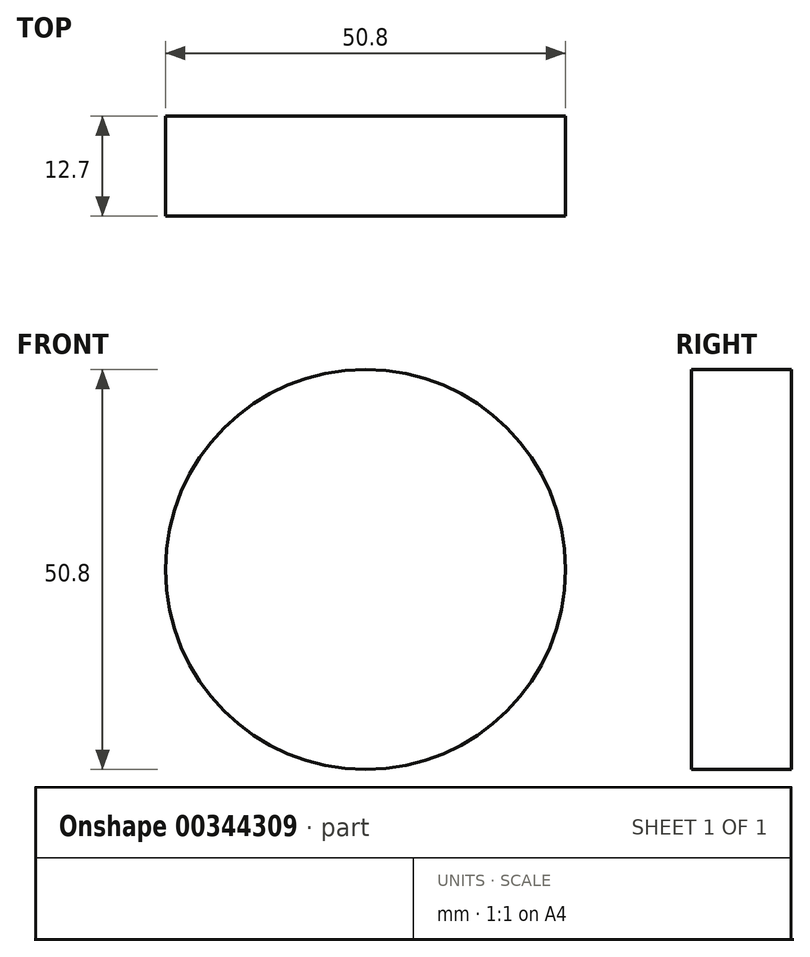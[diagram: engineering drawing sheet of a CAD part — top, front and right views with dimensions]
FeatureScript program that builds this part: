
annotation { "Feature Type Name" : "Feature", "Feature Type Description" : "" }
export const myFeature = defineFeature(function(context is Context, id is Id, definition is map)
    precondition{}
    {
        {
            var Q0;
            Q0=qCreatedBy(makeId("Front.planeOp"),FACE);
            var sketch = newSketch(context, id + "F0", { "sketchPlane" : qUnion([Q0])});
            skCircle(sketch, "E0", {"center": v(0, 0) * mm, "radius": 25.4 * mm});
            skCircle(sketch, "E1", {"center": v(0, 0) * mm, "radius": 16.51 * mm, "construction": true});
            skCircle(sketch, "E2", {"center": v(0, 0) * mm, "radius": 22.86 * mm, "construction": true});
            skLineSegment(sketch, "E3", {"start": v(0, 0) * mm, "end": v(0, 45.4) * mm, "construction": true});
            skLineSegment(sketch, "E4", {"start": v(0, 0) * mm, "end": v(12.17, 45.4) * mm, "construction": true});
            skLineSegment(sketch, "E5", {"start": v(0, 22.86) * mm, "end": v(0, 16.51) * mm});
            skLineSegment(sketch, "E6", {"start": v(5.92, 22.08) * mm, "end": v(4.27, 15.95) * mm});
            skArc(sketch, "E7", {"start": v(0, 22.86) * mm, "mid": v(2.98, 22.66) * mm, "end": v(5.92, 22.08) * mm});
            skArc(sketch, "E8", {"start": v(0, 16.51) * mm, "mid": v(2.15, 16.37) * mm, "end": v(4.27, 15.95) * mm});
            skLineSegment(sketch, "E9.1.0", {"start": v(-19.8, 11.43) * mm, "end": v(-14.3, 8.26) * mm});
            skLineSegment(sketch, "E9.1.1", {"start": v(-16.16, 16.16) * mm, "end": v(-11.67, 11.67) * mm});
            skArc(sketch, "E9.1.2", {"start": v(-19.8, 11.43) * mm, "mid": v(-18.14, 13.92) * mm, "end": v(-16.16, 16.16) * mm});
            skArc(sketch, "E9.1.3", {"start": v(-14.3, 8.26) * mm, "mid": v(-13.1, 10.05) * mm, "end": v(-11.67, 11.67) * mm});
            skLineSegment(sketch, "E9.2.0", {"start": v(-19.8, -11.43) * mm, "end": v(-14.3, -8.25) * mm});
            skLineSegment(sketch, "E9.2.1", {"start": v(-22.08, -5.92) * mm, "end": v(-15.95, -4.27) * mm});
            skArc(sketch, "E9.2.2", {"start": v(-19.8, -11.43) * mm, "mid": v(-21.12, -8.75) * mm, "end": v(-22.08, -5.92) * mm});
            skArc(sketch, "E9.2.3", {"start": v(-14.3, -8.25) * mm, "mid": v(-15.25, -6.32) * mm, "end": v(-15.95, -4.27) * mm});
            skLineSegment(sketch, "E9.3.0", {"start": v(0, -22.86) * mm, "end": v(0, -16.51) * mm});
            skLineSegment(sketch, "E9.3.1", {"start": v(-5.92, -22.08) * mm, "end": v(-4.27, -15.95) * mm});
            skArc(sketch, "E9.3.2", {"start": v(0, -22.86) * mm, "mid": v(-2.98, -22.66) * mm, "end": v(-5.92, -22.08) * mm});
            skArc(sketch, "E9.3.3", {"start": v(0, -16.51) * mm, "mid": v(-2.15, -16.37) * mm, "end": v(-4.27, -15.95) * mm});
            skLineSegment(sketch, "E9.4.0", {"start": v(19.8, -11.43) * mm, "end": v(14.3, -8.26) * mm});
            skLineSegment(sketch, "E9.4.1", {"start": v(16.16, -16.16) * mm, "end": v(11.67, -11.67) * mm});
            skArc(sketch, "E9.4.2", {"start": v(19.8, -11.43) * mm, "mid": v(18.14, -13.92) * mm, "end": v(16.16, -16.16) * mm});
            skArc(sketch, "E9.4.3", {"start": v(14.3, -8.26) * mm, "mid": v(13.1, -10.05) * mm, "end": v(11.67, -11.67) * mm});
            skLineSegment(sketch, "E9.5.0", {"start": v(19.8, 11.43) * mm, "end": v(14.3, 8.26) * mm});
            skLineSegment(sketch, "E9.5.1", {"start": v(22.08, 5.92) * mm, "end": v(15.95, 4.27) * mm});
            skArc(sketch, "E9.5.2", {"start": v(19.8, 11.43) * mm, "mid": v(21.12, 8.75) * mm, "end": v(22.08, 5.92) * mm});
            skArc(sketch, "E9.5.3", {"start": v(14.3, 8.26) * mm, "mid": v(15.25, 6.32) * mm, "end": v(15.95, 4.27) * mm});
            skSolve(sketch);
        }
        {
            var Q0;
            Q0=makeQuery(id+"F0.imprint","IMPRINT",FACE,{"disambiguationData":[TD([[makeQuery(id+"F0.imprint","IMPRINT",EDGE,{"derivedFrom":sQuery(id+"F0.wireOp",EDGE,"RZoZ2ge6-8GLw-KyjR-YQcm-iaacOE0NIIhm")}),-1.0]])]});
            var Q1;
            Q1=makeQuery(id+"F0.imprint","IMPRINT",FACE,{"disambiguationData":[TD([[makeQuery(id+"F0.imprint","IMPRINT",EDGE,{"derivedFrom":sQuery(id+"F0.wireOp",EDGE,"E0")}),1.0]])]});
            var Q2;
            Q2=makeQuery(id+"F0.imprint","IMPRINT",FACE,{"disambiguationData":[TD([[makeQuery(id+"F0.imprint","IMPRINT",EDGE,{"derivedFrom":sQuery(id+"F0.wireOp",EDGE,"E5")}),1.0]])]});
            var Q3;
            Q3=makeQuery(id+"F0.imprint","IMPRINT",FACE,{"disambiguationData":[TD([[makeQuery(id+"F0.imprint","IMPRINT",EDGE,{"derivedFrom":sQuery(id+"F0.wireOp",EDGE,"E9.1.0")}),1.0]])]});
            var Q4;
            Q4=makeQuery(id+"F0.imprint","IMPRINT",FACE,{"disambiguationData":[TD([[makeQuery(id+"F0.imprint","IMPRINT",EDGE,{"derivedFrom":sQuery(id+"F0.wireOp",EDGE,"E9.2.0")}),1.0]])]});
            var Q5;
            Q5=makeQuery(id+"F0.imprint","IMPRINT",FACE,{"disambiguationData":[TD([[makeQuery(id+"F0.imprint","IMPRINT",EDGE,{"derivedFrom":sQuery(id+"F0.wireOp",EDGE,"E9.4.0")}),1.0]])]});
            var Q6;
            Q6=makeQuery(id+"F0.imprint","IMPRINT",FACE,{"disambiguationData":[TD([[makeQuery(id+"F0.imprint","IMPRINT",EDGE,{"derivedFrom":sQuery(id+"F0.wireOp",EDGE,"E9.5.0")}),1.0]])]});
            var Q7;
            Q7=makeQuery(id+"F0.imprint","IMPRINT",FACE,{"disambiguationData":[TD([[makeQuery(id+"F0.imprint","IMPRINT",EDGE,{"derivedFrom":sQuery(id+"F0.wireOp",EDGE,"E9.3.0")}),1.0]])]});
            extrude(context, id + "F1", {"entities" : qUnion([Q0, Q1, Q2, Q3, Q4, Q5, Q6, Q7]), "depth" : 12.7 * mm});
        }
        {
            var Q0;
            Q0=makeQuery(id+"F0.imprint","IMPRINT",FACE,{"disambiguationData":[TD([[makeQuery(id+"F0.imprint","IMPRINT",EDGE,{"derivedFrom":sQuery(id+"F0.wireOp",EDGE,"E9.5.0")}),1.0]])]});
            var Q1;
            Q1=makeQuery(id+"F0.imprint","IMPRINT",FACE,{"disambiguationData":[TD([[makeQuery(id+"F0.imprint","IMPRINT",EDGE,{"derivedFrom":sQuery(id+"F0.wireOp",EDGE,"E9.4.0")}),1.0]])]});
            var Q2;
            Q2=makeQuery(id+"F0.imprint","IMPRINT",FACE,{"disambiguationData":[TD([[makeQuery(id+"F0.imprint","IMPRINT",EDGE,{"derivedFrom":sQuery(id+"F0.wireOp",EDGE,"E9.3.0")}),1.0]])]});
            var Q3;
            Q3=makeQuery(id+"F0.imprint","IMPRINT",FACE,{"disambiguationData":[TD([[makeQuery(id+"F0.imprint","IMPRINT",EDGE,{"derivedFrom":sQuery(id+"F0.wireOp",EDGE,"E9.1.0")}),1.0]])]});
            var Q4;
            Q4=makeQuery(id+"F0.imprint","IMPRINT",FACE,{"disambiguationData":[TD([[makeQuery(id+"F0.imprint","IMPRINT",EDGE,{"derivedFrom":sQuery(id+"F0.wireOp",EDGE,"E5")}),1.0]])]});
            var Q5;
            Q5=makeQuery(id+"F0.imprint","IMPRINT",FACE,{"disambiguationData":[TD([[makeQuery(id+"F0.imprint","IMPRINT",EDGE,{"derivedFrom":sQuery(id+"F0.wireOp",EDGE,"E9.2.0")}),1.0]])]});
            extrude(context, id + "F2", {"entities" : qUnion([Q0, Q1, Q2, Q3, Q4, Q5]), "operationType" : NewBodyOperationType.ADD, "depth" : 5 / 203.2 * mm});
        }
    });
